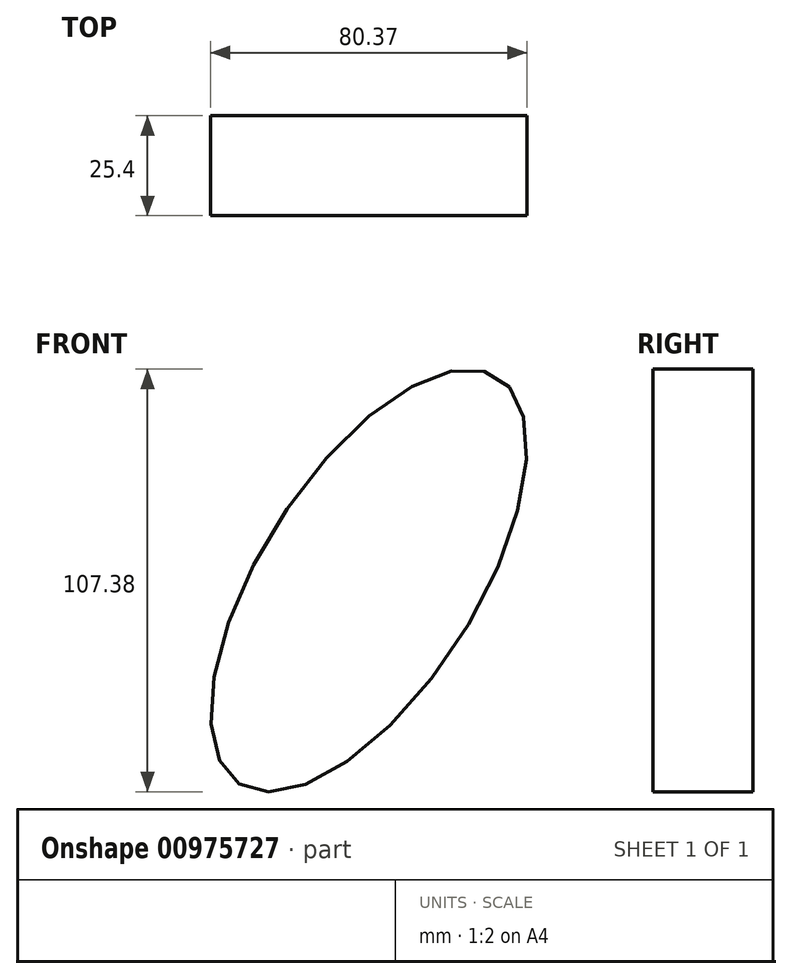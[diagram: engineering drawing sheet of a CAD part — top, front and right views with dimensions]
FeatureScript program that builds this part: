
annotation { "Feature Type Name" : "Feature", "Feature Type Description" : "" }
export const myFeature = defineFeature(function(context is Context, id is Id, definition is map)
    precondition{}
    {
        {
            var Q0;
            Q0=qCreatedBy(makeId("Front.planeOp"),FACE);
            var sketch = newSketch(context, id + "F0", { "sketchPlane" : qUnion([Q0])});
            skEllipse(sketch, "E0", {"center": v(47.74, 37.28) * mm, "majorRadius": 27.38 * mm, "minorRadius": 61.22 * mm, "majorAxis": v(-0.84, 0.54)});
            skSolve(sketch);
        }
        {
            var Q0;
            Q0=sQuery(id+"F0.wireOp",EDGE,"E0");
            extrude(context, id + "F1", {"bodyType" : ToolBodyType.SURFACE, "surfaceEntities" : qUnion([Q0]), "depth" : 25.4 * mm, "offsetDistance" : 25.4 * mm});
        }
    });
